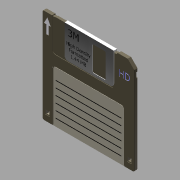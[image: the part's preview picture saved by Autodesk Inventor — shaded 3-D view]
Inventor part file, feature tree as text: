
AUTODESK INVENTOR PART (.ipt)
format: ipt  version: 2011 SP2 (Build 150309200, 309)  size: 1,358,336 bytes
history: native  units: in
note: dims shown in document units (in); Inventor stores cm internally (conversion verified against a paired STEP export)
features: sketch x28, extrude x24, emboss x4, plane x1, mirror x1, fillet x1, projected_geometry x1
ambient origin geometry x8: Origin, YZ Plane, XZ Plane, XY Plane, X Axis, Y Axis, Z Axis, Center Point
bodies: Solid1 (feature_tree)
feature tree (60):
  extrude  "Extrusion1"  Depth=3.625in
  extrude  "Extrusion2"  Depth=0.25in
  extrude  "Extrusion3"  Depth=0.125in TaperAngle=0.0deg
  extrude  "Extrusion4"  Depth=0.25in
  extrude  "Extrusion5"  Depth=0.125in
  extrude  "Extrusion6"  Depth=0.0312in
  extrude  "Extrusion7"  Depth=0.0156in TaperAngle=0.0deg
  extrude  "Extrusion8"  Depth=2.0in
  extrude  "Extrusion9"  Depth=0.0156in TaperAngle=0.0deg
  extrude  "Extrusion10"  Depth=0.5in
  plane  "Work Plane1"
  mirror  "Mirror1"
  extrude  "Extrusion11"  TaperAngle=0.0deg  [1 undecoded]
  extrude  "Extrusion12"  TaperAngle=0.0deg  [1 undecoded]
  extrude  "Extrusion13"  Depth=0.125in
  emboss  "Emboss1"
  emboss  "Emboss2"
  extrude  "Extrusion14"  Depth=2.375in
  extrude  "Extrusion15"  TaperAngle=0.0deg  [1 undecoded]
  extrude  "Extrusion16"  Depth=0.125in
  extrude  "Extrusion17"  Depth=0.0625in
  extrude  "Extrusion18"  Depth=0.0156in
  emboss  "Emboss3"
  extrude  "Extrusion19"  Depth=1.875in
  extrude  "Extrusion20"  Depth=0.0312in
  sketch  "Sketch25"  dims[d57=0.0312in d58=0.0156in]
  fillet  "Fillet1"  Radius=0.125in
  emboss  "Emboss4"
  extrude  "Extrusion21"  Depth=0.5in
  extrude  "Extrusion22"  Depth=0.0312in
  extrude  "Extrusion23"  TaperAngle=0.0deg  [1 undecoded]
  extrude  "Extrusion24"  Depth=0.0156in
  sketch  "Sketch1"  dims[d0=3.5in d1=3.625in]
  sketch  "Sketch2"  dims[d2=0.25in d3=0.25in]
  sketch  "Sketch3"  dims[d4=0.0625in d5=0.125in d6=0.0in]
  sketch  "Sketch4"  dims[d7=0.125in d8=0.25in]
  sketch  "Sketch5"  dims[d9=0.125in d10=0.125in]
  sketch  "Sketch6"  dims[d11=0.125in d12=0.0in d13=0.0312in]
  sketch  "Sketch7"  dims[d14=0.0312in d15=0.0156in d16=0.0in]
  sketch  "Sketch8"  dims[d17=2.75in d18=2.0in]
  sketch  "Sketch10"  dims[d19=0.125in d20=0.0156in d21=0.0in]
  sketch  "Sketch11"  dims[d22=0.0156in d23=0.0in d24=0.5in]
  sketch  "Sketch12"  dims[d25=0.0156in d26=0.0in]
  sketch  "Sketch13"  dims[d27=0.0156in d28=0.0in]
  sketch  "Sketch14"  dims[d29=0.125in d31=0.125in]
  sketch  "Sketch15"  dims[d32=1.25in d33=2.375in]
  sketch  "Sketch16"  dims[d34=0.0156in d35=0.0in]
  sketch  "Sketch17"  dims[d40=0.0312in d41=0.125in]
  sketch  "Sketch18"  dims[d42=45.0deg d43=0.0625in]
  sketch  "Sketch19"  dims[d44=0.125in d45=0.0156in]
  sketch  "Sketch20"  dims[d46=0.0in d47=1.875in]
  sketch  "Sketch21"  dims[d48=0.125in d49=0.0312in d50=0.125in]
  sketch  "Sketch22"  dims[d51=0.9375in d52=0.5in]
  sketch  "Sketch23"  dims[d53=0.3125in d54=0.0312in]
  sketch  "Sketch24"  dims[d55=0.0156in d56=0.0in]
  sketch  "Sketch26"  dims[d59=0.0in]
  sketch  "Sketch27"  dims[d60=0.0156in]
  sketch  "Sketch28"  dims[d61=0.0in]
  sketch  "Sketch29"  dims[d62=0.0156in d63=0.0in d64=0.01in d65=0.0in d66=0.01in d67=0.0in d68=1.625in d69=1.0in d70=0.0938in d71=0.0in d72=0.9375in d73=0.0312in d74=0.125in d75=0.125in d76=0.25in d77=0.0312in d78=0.0938in d79=0.0in d80=0.0938in d81=0.0in d82=0.125in d83=0.13in d84=0.01in d85=0.0938in d86=0.0in d87=0.012in d88=0.012in d89=0.012in d90=0.012in d91=0.0156in d92=0.0in d93=0.01in d94=0.0in d95=0.2in d96=0.0469in d97=0.0in d98=0.15in d99=0.15in d100=0.15in d101=0.0469in d102=0.0in d103=0.0156in d104=0.001in d105=0.0in d106=0.0312in d107=0.0312in d108=0.0312in d109=0.0312in d110=0.01in d111=0.0in d112=0.0312in d113=0.0312in d114=0.01in d115=0.0in d116=0.01in d117=0.0in d118=2.3622in d120=0.25in d121=0.3937in d123=1.0in d125=0.001in d126=0.0in]
  projected_geometry  "Project Cut Edges2"
note: 4 required parameter values undecoded (feature->parameter linkage not recoverable at this tier; creation-order binding heuristic only, values carry confidence <= 0.55)
